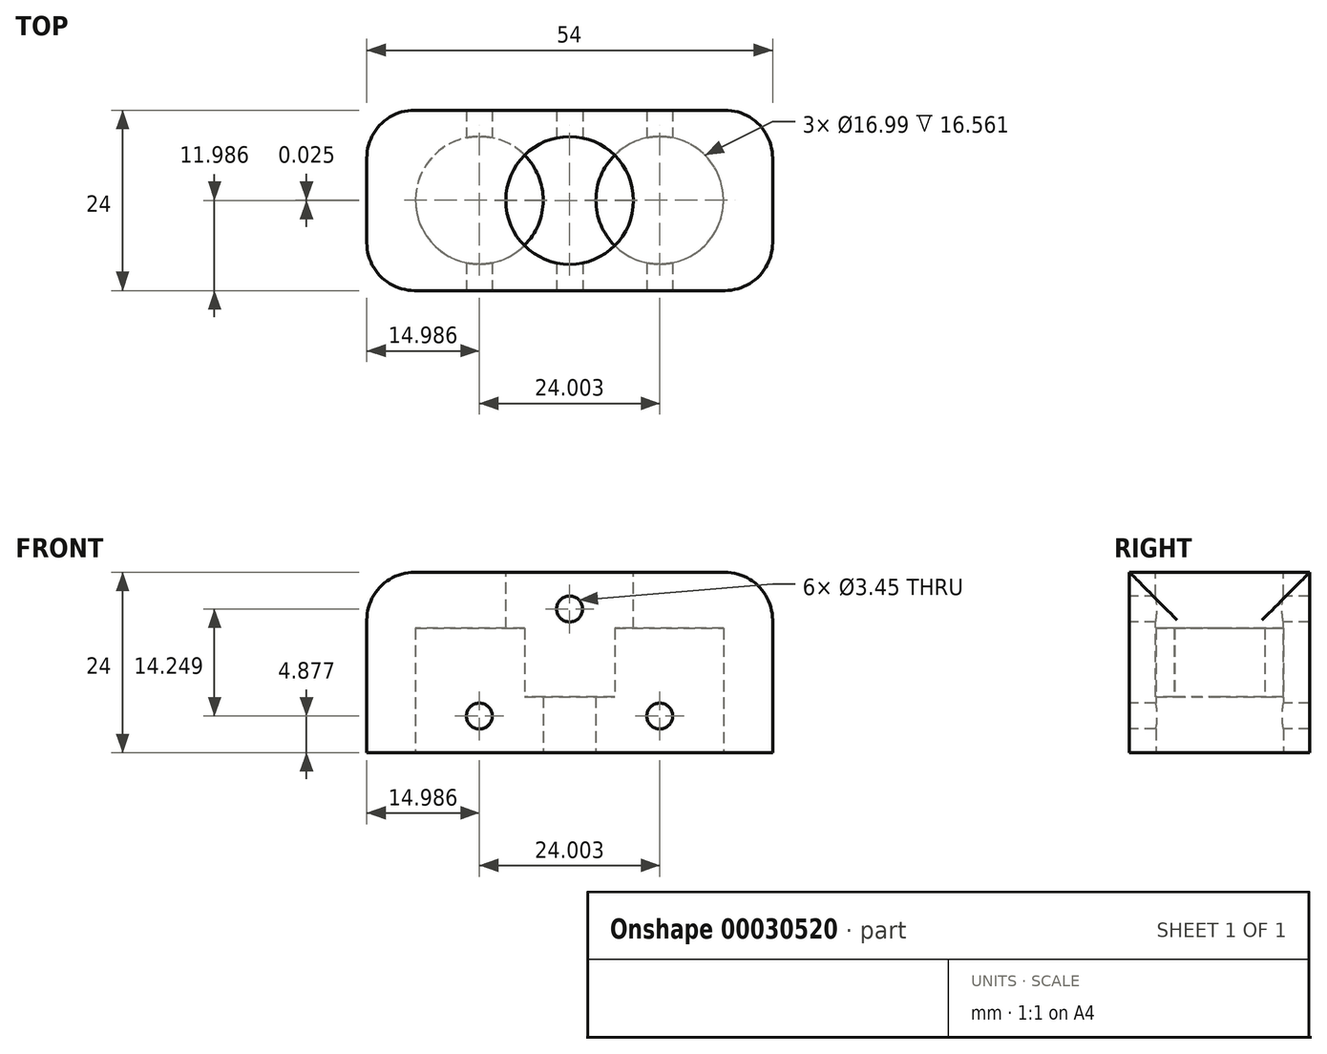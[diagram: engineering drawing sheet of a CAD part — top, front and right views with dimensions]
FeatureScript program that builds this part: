
annotation { "Feature Type Name" : "Feature", "Feature Type Description" : "" }
export const myFeature = defineFeature(function(context is Context, id is Id, definition is map)
    precondition{}
    {
        {
            var Q0;
            Q0=qCreatedBy(makeId("Front.planeOp"),FACE);
            var sketch = newSketch(context, id + "F0", { "sketchPlane" : qUnion([Q0])});
            skLineSegment(sketch, "E0.bottom", {"start": v(0, 0) * mm, "end": v(54, 0) * mm});
            skLineSegment(sketch, "E0.top", {"start": v(0, 24) * mm, "end": v(54, 24) * mm});
            skLineSegment(sketch, "E0.left", {"start": v(0, 0) * mm, "end": v(0, 24) * mm});
            skLineSegment(sketch, "E0.right", {"start": v(54, 0) * mm, "end": v(54, 24) * mm});
            skSolve(sketch);
        }
        {
            var Q0;
            Q0 = qSketchRegion(id + "F0", true);
            extrude(context, id + "F1", {"entities" : qUnion([Q0]), "depth" : 24 * mm});
        }
        {
            var Q0;
            Q0=makeQuery(id+"F1.opExtrude","SWEPT_FACE",FACE,{"disambiguationData":[OSD([sQuery(id+"F0.wireOp",EDGE,"E0.top")])]});
            var sketch = newSketch(context, id + "F2", { "sketchPlane" : qUnion([Q0])});
            skCircle(sketch, "E1", {"center": v(27, -12.01) * mm, "radius": 8.5 * mm});
            skSolve(sketch);
        }
        {
            var Q0;
            Q0 = qSketchRegion(id + "F2", true);
            extrude(context, id + "F6", {"entities" : qUnion([Q0]), "operationType" : NewBodyOperationType.REMOVE, "oppositeDirection" : true, "depth" : 16.56 * mm});
        }
        {
            var Q0;
            Q0=makeQuery(id+"F1.opExtrude","SWEPT_FACE",FACE,{"disambiguationData":[OSD([sQuery(id+"F0.wireOp",EDGE,"E0.bottom")])]});
            var sketch = newSketch(context, id + "F7", { "sketchPlane" : qUnion([Q0])});
            skCircle(sketch, "E2", {"center": v(14.99, 11.99) * mm, "radius": 8.5 * mm});
            skCircle(sketch, "E3", {"center": v(38.99, 11.99) * mm, "radius": 8.5 * mm});
            skSolve(sketch);
        }
        {
            var Q0;
            Q0 = qSketchRegion(id + "F7", true);
            extrude(context, id + "F8", {"entities" : qUnion([Q0]), "operationType" : NewBodyOperationType.REMOVE, "oppositeDirection" : true, "depth" : 16.56 * mm});
        }
        {
            var Q0;
            Q0=makeQuery(id+"F1.opExtrude","SWEPT_EDGE",EDGE,{"disambiguationData":[OSD([sQuery(id+"F0.wireOp",EDGE,"E0.top"),sQuery(id+"F0.wireOp",EDGE,"E0.right")])]});
            var Q1;
            Q1=makeQuery(id+"F1.opExtrude","SWEPT_EDGE",EDGE,{"disambiguationData":[OSD([sQuery(id+"F0.wireOp",EDGE,"E0.top"),sQuery(id+"F0.wireOp",EDGE,"E0.left")])]});
            fillet(context, id + "F3", {"entities" : qUnion([Q0, Q1]), "radius" : 6.35 * mm, "allowEdgeOverflow" : false});
        }
        {
            var Q0;
            Q0=makeQuery(id+"F1.opExtrude","CAP_EDGE",EDGE,{"disambiguationData":[OSD([sQuery(id+"F0.wireOp",EDGE,"E0.right")])],"isStart":false});
            var Q1;
            Q1=makeQuery(id+"F1.opExtrude","CAP_EDGE",EDGE,{"disambiguationData":[OSD([sQuery(id+"F0.wireOp",EDGE,"E0.right")])],"isStart":true});
            var Q2;
            Q2=makeQuery(id+"F1.opExtrude","CAP_EDGE",EDGE,{"disambiguationData":[OSD([sQuery(id+"F0.wireOp",EDGE,"E0.left")])],"isStart":false});
            var Q3;
            Q3=makeQuery(id+"F1.opExtrude","CAP_EDGE",EDGE,{"disambiguationData":[OSD([sQuery(id+"F0.wireOp",EDGE,"E0.left")])],"isStart":true});
            fillet(context, id + "F4", {"entities" : qUnion([Q0, Q1, Q2, Q3]), "radius" : 6.35 * mm, "allowEdgeOverflow" : false});
        }
        {
            var Q0;
            Q0=makeQuery(id+"F1.opExtrude","CAP_FACE",FACE,{"disambiguationData":[OSD([sQuery(id+"F0.wireOp",EDGE,"E0.bottom"),sQuery(id+"F0.wireOp",EDGE,"E0.top"),sQuery(id+"F0.wireOp",EDGE,"E0.left"),sQuery(id+"F0.wireOp",EDGE,"E0.right")])],"isStart":false});
            var sketch = newSketch(context, id + "F9", { "sketchPlane" : qUnion([Q0])});
            skPoint(sketch, "E4", {"position": v(27, 19.13) * mm});
            skPoint(sketch, "E5", {"position": v(14.99, 4.88) * mm});
            skPoint(sketch, "E6", {"position": v(38.99, 4.88) * mm});
            skSolve(sketch);
        }
        {
            var Q0;
            Q0=sQuery(id+"F9.wireOp",VERTEX,"E4");
            var Q1;
            Q1=sQuery(id+"F9.wireOp",VERTEX,"E6");
            var Q2;
            Q2=sQuery(id+"F9.wireOp",VERTEX,"E5");
            var Q3;
            Q3=makeQuery(id+"F1.opExtrude","SWEPT_BODY",BODY,{"disambiguationData":[OSD([sQuery(id+"F0.wireOp",EDGE,"E0.bottom"),sQuery(id+"F0.wireOp",EDGE,"E0.top"),sQuery(id+"F0.wireOp",EDGE,"E0.left"),sQuery(id+"F0.wireOp",EDGE,"E0.right")])]});
            hole(context, id + "F5", {"style" : HoleStyle.SIMPLE, "holeDiameter" : 3.45 * mm, "endStyle" : HoleEndStyle.THROUGH, "locations" : qUnion([Q0, Q1, Q2]), "scope" : qUnion([Q3]), "standardTappedOrClearance" : lookupTablePath({ "standard" : "ANSI", "engagement" : "75%", "pitch" : "32 tpi", "size" : "#8", "type" : "Tapped" }), "standardBlindInLast" : lookupTablePath({ "standard" : "ANSI", "engagement" : "75%", "pitch" : "32 tpi", "size" : "#8", "type" : "Tapped" }), "isTappedThrough" : true, "majorDiameter" : 4.17 * mm, "showTappedDepth" : true});
        }
    });
